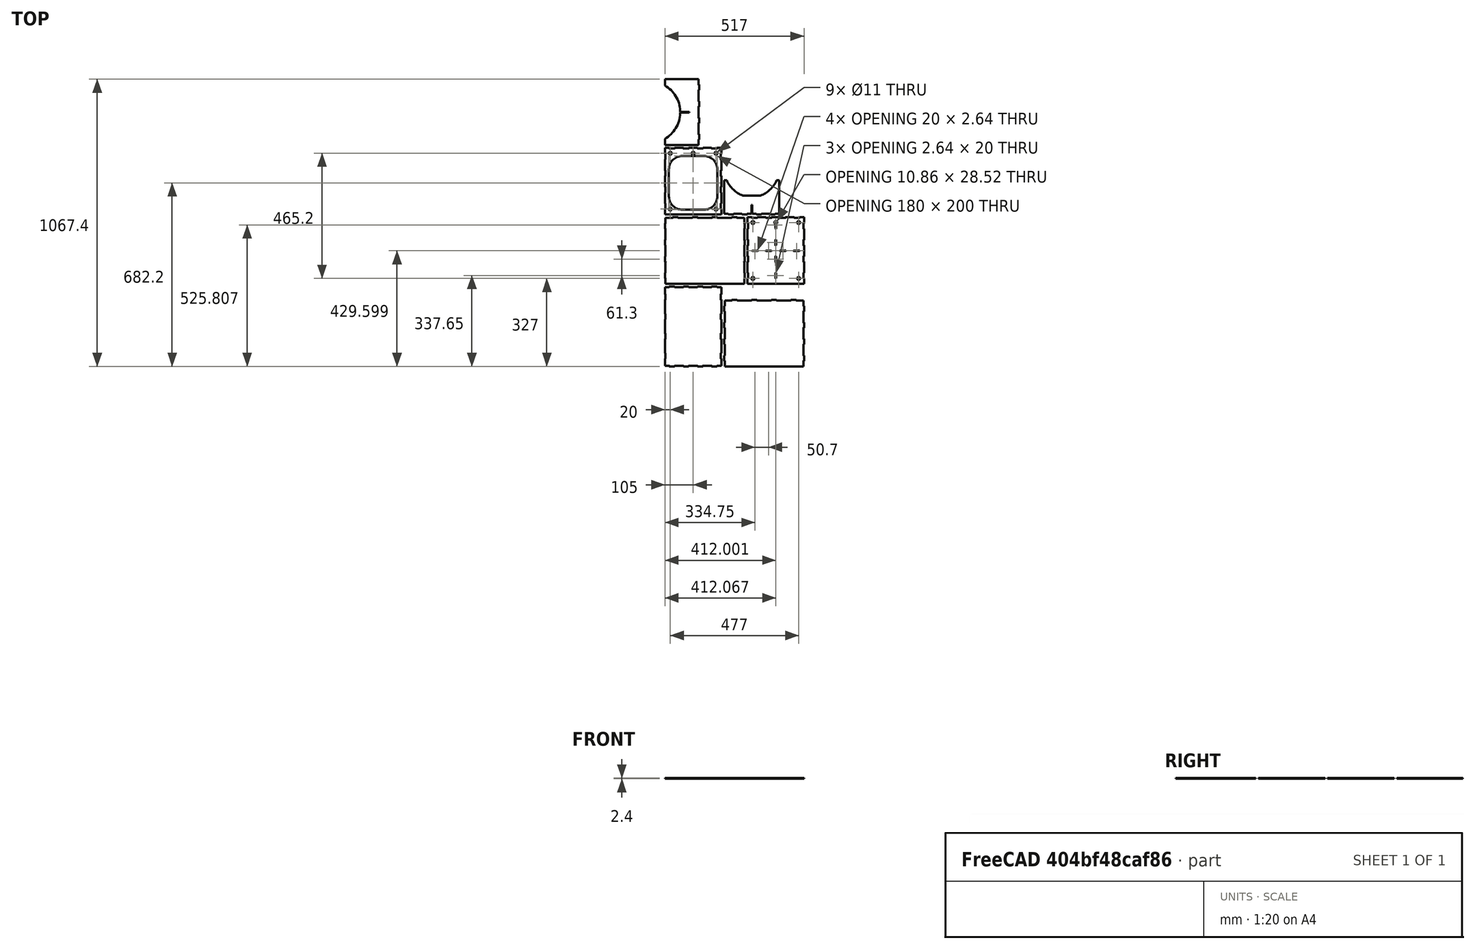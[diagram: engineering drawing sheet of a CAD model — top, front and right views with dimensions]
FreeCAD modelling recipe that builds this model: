
FCSTD DOCUMENT  (FreeCAD 1.0R39319 (Git))
Label: magnificator_02_2_4_tabs_MultiJoin_export
License: CERN Open Hardware Licence permissive
LicenseURL: https://cern-ohl.web.cern.ch/
objects: Part::Feature×7, Part::Part2DObjectPython×7
note: 14 computed .brp shape members not serialized (recipe doc carries the construction recipe); baked Part::Feature solids carry a one-line shape summary decoded from their .brp

FEATURE [Part::Feature] test
  Placement = pos=(105,148.5,-217.6) rot=(1,0,0;1.5708rad)
  shape: bbox 210 x 297 x 2.4 mm, 102 faces (baked)
FEATURE [Part::Feature] test001
  Placement = pos=(368.5,-2.4,-72.6) rot=(0,-1,0;1.5708rad)
  shape: bbox 297 x 247.6 x 2.4 mm, 78 faces (baked)
FEATURE [Part::Feature] test002
  Placement = pos=(148.5,304.6,-72.6) rot=(0,1,0;1.5708rad)
  shape: bbox 297 x 247.6 x 2.4 mm, 78 faces (baked)
FEATURE [Part::Feature] test003
  Placement = pos=(412,304.6,-116.1) rot=(0,0,1;0rad)
  shape: bbox 210 x 247.6 x 2.4 mm, 144 faces (baked)
FEATURE [Part::Feature] test004
  Placement = pos=(105,562.2,-116.1) rot=(0,-1,0;3.14159rad)
  shape: bbox 210 x 247.6 x 2.401 mm, 91 faces (baked)
FEATURE [Part::Feature] test005
  Placement = pos=(322.6,713.1,-93.8) rot=(1,0,0;1.5708rad)
  shape: bbox 205.2 x 127.4 x 2.4 mm, 38 faces (baked)
FEATURE [Part::Feature] test006
  Placement = pos=(-21.1,819.8,31.2) rot=(0,1,0;1.5708rad)
  shape: bbox 127.4 x 245.2 x 2.4 mm, 38 faces (baked)
FEATURE [Part::Part2DObjectPython] Shape2DView  # Draft 2D object (typed FeaturePython)
  AutoUpdate = true
  Base = -> test
  Clip = false
  FuseArch = false
  HiddenLines = false
  InPlace = true
  OnlySolids = false
  Projection = (0,0,1)
  ProjectionMode = 0
  SegmentLength = 0.05
  Tessellation = false
  VisibleOnly = false
FEATURE [Part::Part2DObjectPython] Shape2DView001  # Draft 2D object (typed FeaturePython)
  AutoUpdate = true
  Base = -> test001
  Clip = false
  FuseArch = false
  HiddenLines = false
  InPlace = true
  OnlySolids = false
  Projection = (0,0,1)
  ProjectionMode = 0
  SegmentLength = 0.05
  Tessellation = false
  VisibleOnly = false
FEATURE [Part::Part2DObjectPython] Shape2DView002  # Draft 2D object (typed FeaturePython)
  AutoUpdate = true
  Base = -> test002
  Clip = false
  FuseArch = false
  HiddenLines = false
  InPlace = true
  OnlySolids = false
  Projection = (0,0,1)
  ProjectionMode = 0
  SegmentLength = 0.05
  Tessellation = false
  VisibleOnly = false
FEATURE [Part::Part2DObjectPython] Shape2DView003  # Draft 2D object (typed FeaturePython)
  AutoUpdate = true
  Base = -> test003
  Clip = false
  FuseArch = false
  HiddenLines = false
  InPlace = true
  OnlySolids = false
  Projection = (0,0,1)
  ProjectionMode = 0
  SegmentLength = 0.05
  Tessellation = false
  VisibleOnly = false
FEATURE [Part::Part2DObjectPython] Shape2DView004  # Draft 2D object (typed FeaturePython)
  AutoUpdate = true
  Base = -> test004
  Clip = false
  FuseArch = false
  HiddenLines = false
  InPlace = true
  OnlySolids = false
  Projection = (0,0,1)
  ProjectionMode = 0
  SegmentLength = 0.05
  Tessellation = false
  VisibleOnly = false
FEATURE [Part::Part2DObjectPython] Shape2DView005  # Draft 2D object (typed FeaturePython)
  AutoUpdate = true
  Base = -> test005
  Clip = false
  FuseArch = false
  HiddenLines = false
  InPlace = true
  OnlySolids = false
  Projection = (0,0,1)
  ProjectionMode = 0
  SegmentLength = 0.05
  Tessellation = false
  VisibleOnly = false
FEATURE [Part::Part2DObjectPython] Shape2DView006  # Draft 2D object (typed FeaturePython)
  AutoUpdate = true
  Base = -> test006
  Clip = false
  FuseArch = false
  HiddenLines = false
  InPlace = true
  OnlySolids = false
  Projection = (0,0,1)
  ProjectionMode = 0
  SegmentLength = 0.05
  Tessellation = false
  VisibleOnly = false
